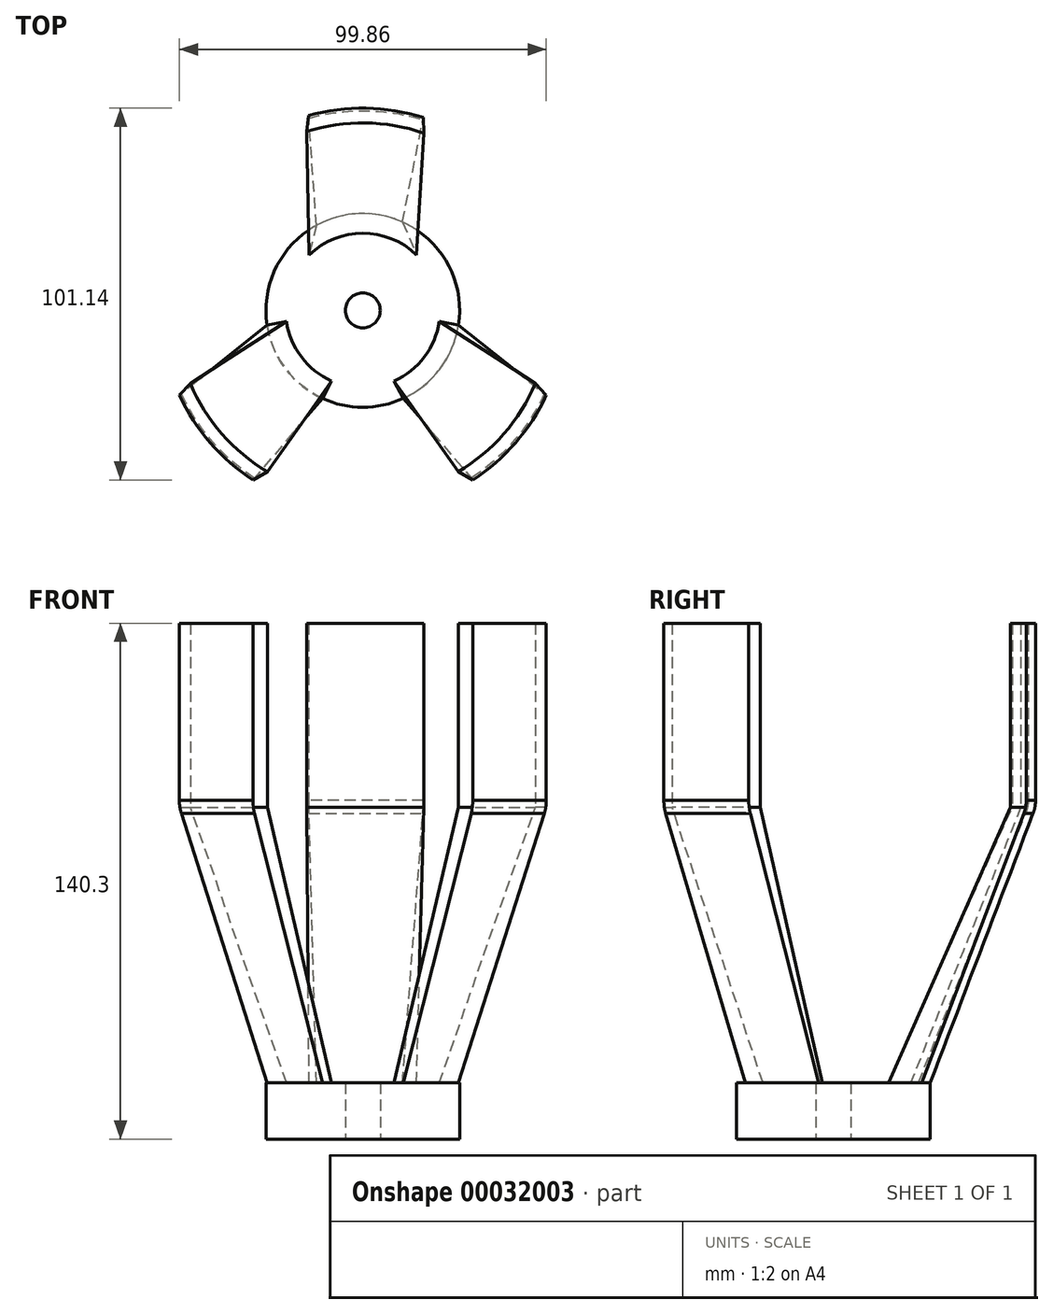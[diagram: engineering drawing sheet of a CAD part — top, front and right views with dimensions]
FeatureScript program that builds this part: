
annotation { "Feature Type Name" : "Feature", "Feature Type Description" : "" }
export const myFeature = defineFeature(function(context is Context, id is Id, definition is map)
    precondition{}
    {
        {
            var Q0;
            Q0=qCreatedBy(makeId("Top.planeOp"),FACE);
            var sketch = newSketch(context, id + "F0", { "sketchPlane" : qUnion([Q0])});
            skCircle(sketch, "E0", {"center": v(0, 0) * mm, "radius": 26.35 * mm});
            skCircle(sketch, "E1", {"center": v(0, 0) * mm, "radius": 4.75 * mm});
            skSolve(sketch);
        }
        {
            var Q0;
            Q0=makeQuery(id+"F0.imprint","IMPRINT",FACE,{"disambiguationData":[TD([[makeQuery(id+"F0.imprint","IMPRINT",EDGE,{"derivedFrom":sQuery(id+"F0.wireOp",EDGE,"E0")}),1.0]])]});
            extrude(context, id + "F1", {"entities" : qUnion([Q0]), "depth" : 15.3 * mm});
        }
        {
            var Q0;
            Q0=makeQuery(id+"F1.opExtrude","CAP_FACE",FACE,{"disambiguationData":[OSD([sQuery(id+"F0.wireOp",EDGE,"E0"),sQuery(id+"F0.wireOp",EDGE,"E1")])],"isStart":false});
            cPlane(context, id + "F2", {"entities" : qUnion([Q0]), "cplaneType" : CPlaneType.OFFSET, "offset" : 0 * mm, "width" : 150 * mm, "height" : 150 * mm});
        }
        {
            var Q0;
            Q0=qCreatedBy(id+"F2.planeOp",FACE);
            var sketch = newSketch(context, id + "F3", { "sketchPlane" : qUnion([Q0])});
            skCircle(sketch, "E2.0", {"center": v(0, 0) * mm, "radius": 26.35 * mm});
            skCircle(sketch, "E3", {"center": v(0, 0) * mm, "radius": 21 * mm});
            skLineSegment(sketch, "E4", {"start": v(-12.64, 23.12) * mm, "end": v(-14.62, 15.07) * mm});
            skLineSegment(sketch, "E5", {"start": v(10.8, 24.03) * mm, "end": v(14.62, 15.07) * mm});
            skLineSegment(sketch, "E6", {"start": v(-20.78, -3) * mm, "end": v(-26.04, -4) * mm});
            skLineSegment(sketch, "E7", {"start": v(-8.5, -19.2) * mm, "end": v(-11, -23.94) * mm});
            skLineSegment(sketch, "E8", {"start": v(8.5, -19.2) * mm, "end": v(11, -23.94) * mm});
            skLineSegment(sketch, "E9", {"start": v(20.78, -3) * mm, "end": v(26.04, -4) * mm});
            skSolve(sketch);
        }
        {
            var Q0;
            {var subQ0=sQuery(id+"F3.wireOp",EDGE,"E3");var subQ6=makeQuery(id+"F3.imprint","INTERSECT",VERTEX,{"derivedFrom":[subQ0,sQuery(id+"F3.wireOp",EDGE,"E4")]});Q0=makeQuery(id+"F3.imprint","IMPRINT",FACE,{"disambiguationData":[TD([[makeQuery(id+"F3.imprint","IMPRINT",EDGE,{"disambiguationData":[TD([[subQ6,1.0]])],"derivedFrom":subQ0}),1.0]])]});}
            cPlane(context, id + "F4", {"entities" : qUnion([Q0]), "cplaneType" : CPlaneType.OFFSET, "offset" : 75 * mm, "width" : 150 * mm, "height" : 150 * mm});
        }
        {
            var Q0;
            Q0=qCreatedBy(id+"F4.planeOp",FACE);
            var sketch = newSketch(context, id + "F5", { "sketchPlane" : qUnion([Q0])});
            skCircle(sketch, "E10", {"center": v(0, 0) * mm, "radius": 55 * mm});
            skCircle(sketch, "E11", {"center": v(0, 0) * mm, "radius": 51 * mm});
            skLineSegment(sketch, "E12", {"start": v(-14.75, 52.99) * mm, "end": v(-15.33, 48.64) * mm});
            skLineSegment(sketch, "E13", {"start": v(16.46, 52.48) * mm, "end": v(16.57, 48.23) * mm});
            skLineSegment(sketch, "E14", {"start": v(-49.93, -23.07) * mm, "end": v(-46.95, -19.92) * mm});
            skLineSegment(sketch, "E15", {"start": v(-29.93, -46.14) * mm, "end": v(-25.94, -43.91) * mm});
            skLineSegment(sketch, "E16.MirrorCS", {"start": v(29.93, -46.14) * mm, "end": v(25.94, -43.91) * mm});
            skLineSegment(sketch, "E17.MirrorCS", {"start": v(49.93, -23.07) * mm, "end": v(46.95, -19.92) * mm});
            skLineSegment(sketch, "E18", {"start": v(0, 46.8) * mm, "end": v(0, 55) * mm, "construction": true});
            skPoint(sketch, "E18.startSnap0", {"position": v(0, 46.8) * mm});
            skSolve(sketch);
        }
        {
            var Q1;
            {var subQ0=sQuery(id+"F3.wireOp",EDGE,"E6");Q1=makeQuery(id+"F3.imprint","IMPRINT",FACE,{"disambiguationData":[TD([[makeQuery(id+"F3.imprint","IMPRINT",EDGE,{"derivedFrom":subQ0}),1.0]])]});}
            var Q2;
            {var subQ1=sQuery(id+"F5.wireOp",EDGE,"E14");Q2=makeQuery(id+"F5.imprint","IMPRINT",FACE,{"disambiguationData":[TD([[makeQuery(id+"F5.imprint","IMPRINT",EDGE,{"derivedFrom":subQ1}),-1.0]])]});}
            loft(context, id + "F6", {"operationType" : NewBodyOperationType.ADD, "sheetProfilesArray" : [{ "sheetProfileEntities" : qUnion([Q1]) }, { "sheetProfileEntities" : qUnion([Q2]) }]});
        }
        {
            var Q1;
            {var subQ1=sQuery(id+"F3.wireOp",EDGE,"E8");Q1=makeQuery(id+"F3.imprint","IMPRINT",FACE,{"disambiguationData":[TD([[makeQuery(id+"F3.imprint","IMPRINT",EDGE,{"derivedFrom":subQ1}),1.0]])]});}
            var Q2;
            {var subQ1=sQuery(id+"F5.wireOp",EDGE,"E16.MirrorCS");Q2=makeQuery(id+"F5.imprint","IMPRINT",FACE,{"disambiguationData":[TD([[makeQuery(id+"F5.imprint","IMPRINT",EDGE,{"derivedFrom":subQ1}),-1.0]])]});}
            loft(context, id + "F7", {"operationType" : NewBodyOperationType.ADD, "sheetProfilesArray" : [{ "sheetProfileEntities" : qUnion([Q1]) }, { "sheetProfileEntities" : qUnion([Q2]) }]});
        }
        {
            var Q1;
            {var subQ0=sQuery(id+"F3.wireOp",EDGE,"E4");Q1=makeQuery(id+"F3.imprint","IMPRINT",FACE,{"disambiguationData":[TD([[makeQuery(id+"F3.imprint","IMPRINT",EDGE,{"derivedFrom":subQ0}),1.0]])]});}
            var Q2;
            {var subQ1=sQuery(id+"F5.wireOp",EDGE,"E12");Q2=makeQuery(id+"F5.imprint","IMPRINT",FACE,{"disambiguationData":[TD([[makeQuery(id+"F5.imprint","IMPRINT",EDGE,{"derivedFrom":subQ1}),1.0]])]});}
            loft(context, id + "F8", {"operationType" : NewBodyOperationType.ADD, "sheetProfilesArray" : [{ "sheetProfileEntities" : qUnion([Q1]) }, { "sheetProfileEntities" : qUnion([Q2]) }]});
        }
        {
            var Q0;
            Q0=qCreatedBy(id+"F4.planeOp",FACE);
            var sketch = newSketch(context, id + "F9", { "sketchPlane" : qUnion([Q0])});
            skArc(sketch, "E19.0.0", {"start": v(16.46, 52.48) * mm, "mid": v(0.9, 55) * mm, "end": v(-14.75, 52.99) * mm});
            skLineSegment(sketch, "E19.0.1", {"start": v(-14.75, 52.99) * mm, "end": v(-15.33, 48.64) * mm});
            skArc(sketch, "E19.0.2", {"start": v(-15.33, 48.64) * mm, "mid": v(0.65, 51) * mm, "end": v(16.57, 48.23) * mm});
            skLineSegment(sketch, "E19.0.3", {"start": v(16.57, 48.23) * mm, "end": v(16.46, 52.48) * mm});
            skLineSegment(sketch, "E20.0.0", {"start": v(-46.95, -19.92) * mm, "end": v(-49.93, -23.07) * mm});
            skArc(sketch, "E20.0.1", {"start": v(-49.93, -23.07) * mm, "mid": v(-41.56, -36.02) * mm, "end": v(-29.93, -46.14) * mm});
            skLineSegment(sketch, "E20.0.2", {"start": v(-29.93, -46.14) * mm, "end": v(-25.94, -43.91) * mm});
            skArc(sketch, "E20.0.3", {"start": v(-25.94, -43.91) * mm, "mid": v(-38.37, -33.6) * mm, "end": v(-46.95, -19.92) * mm});
            skLineSegment(sketch, "E21.0.0", {"start": v(25.94, -43.91) * mm, "end": v(29.93, -46.14) * mm});
            skArc(sketch, "E21.0.1", {"start": v(29.93, -46.14) * mm, "mid": v(41.56, -36.02) * mm, "end": v(49.93, -23.07) * mm});
            skLineSegment(sketch, "E21.0.2", {"start": v(49.93, -23.07) * mm, "end": v(46.95, -19.92) * mm});
            skArc(sketch, "E21.0.3", {"start": v(46.95, -19.92) * mm, "mid": v(38.37, -33.6) * mm, "end": v(25.94, -43.91) * mm});
            skSolve(sketch);
        }
        {
            var Q0;
            Q0 = qSketchRegion(id + "F9", true);
            extrude(context, id + "F10", {"entities" : qUnion([Q0]), "operationType" : NewBodyOperationType.ADD, "depth" : 50 * mm});
        }
        {
            var Q0;
            Q0=makeQuery(id+"F10.boolean.opBoolean","MERGE",EDGE,{"derivedFrom":[makeQuery(id+"F6.opLoft","MID_CAP_EDGE",EDGE,{"disambiguationData":[OSD([sQuery(id+"F5.wireOp",EDGE,"E10"),sQuery(id+"F5.wireOp",EDGE,"E14"),sQuery(id+"F5.wireOp",EDGE,"E15")])],"capPos":1.0}),makeQuery(id+"F10.opExtrude","CAP_EDGE",EDGE,{"disambiguationData":[OSD([sQuery(id+"F9.wireOp",EDGE,"E20.0.1")])],"isStart":true})]});
            var Q1;
            Q1=makeQuery(id+"F10.boolean.opBoolean","MERGE",EDGE,{"derivedFrom":[makeQuery(id+"F7.opLoft","MID_CAP_EDGE",EDGE,{"disambiguationData":[OSD([sQuery(id+"F5.wireOp",EDGE,"E10"),sQuery(id+"F5.wireOp",EDGE,"E16.MirrorCS"),sQuery(id+"F5.wireOp",EDGE,"E17.MirrorCS")])],"capPos":1.0}),makeQuery(id+"F10.opExtrude","CAP_EDGE",EDGE,{"disambiguationData":[OSD([sQuery(id+"F9.wireOp",EDGE,"E21.0.1")])],"isStart":true})]});
            var Q2;
            Q2=makeQuery(id+"F10.boolean.opBoolean","MERGE",EDGE,{"derivedFrom":[makeQuery(id+"F8.opLoft","MID_CAP_EDGE",EDGE,{"disambiguationData":[OSD([sQuery(id+"F5.wireOp",EDGE,"E10"),sQuery(id+"F5.wireOp",EDGE,"E12"),sQuery(id+"F5.wireOp",EDGE,"E13")])],"capPos":1.0}),makeQuery(id+"F10.opExtrude","CAP_EDGE",EDGE,{"disambiguationData":[OSD([sQuery(id+"F9.wireOp",EDGE,"E19.0.0")])],"isStart":true})]});
            fillet(context, id + "F11", {"entities" : qUnion([Q0, Q1, Q2]), "radius" : 10 * mm, "tangentPropagation" : true, "allowEdgeOverflow" : false});
        }
    });
